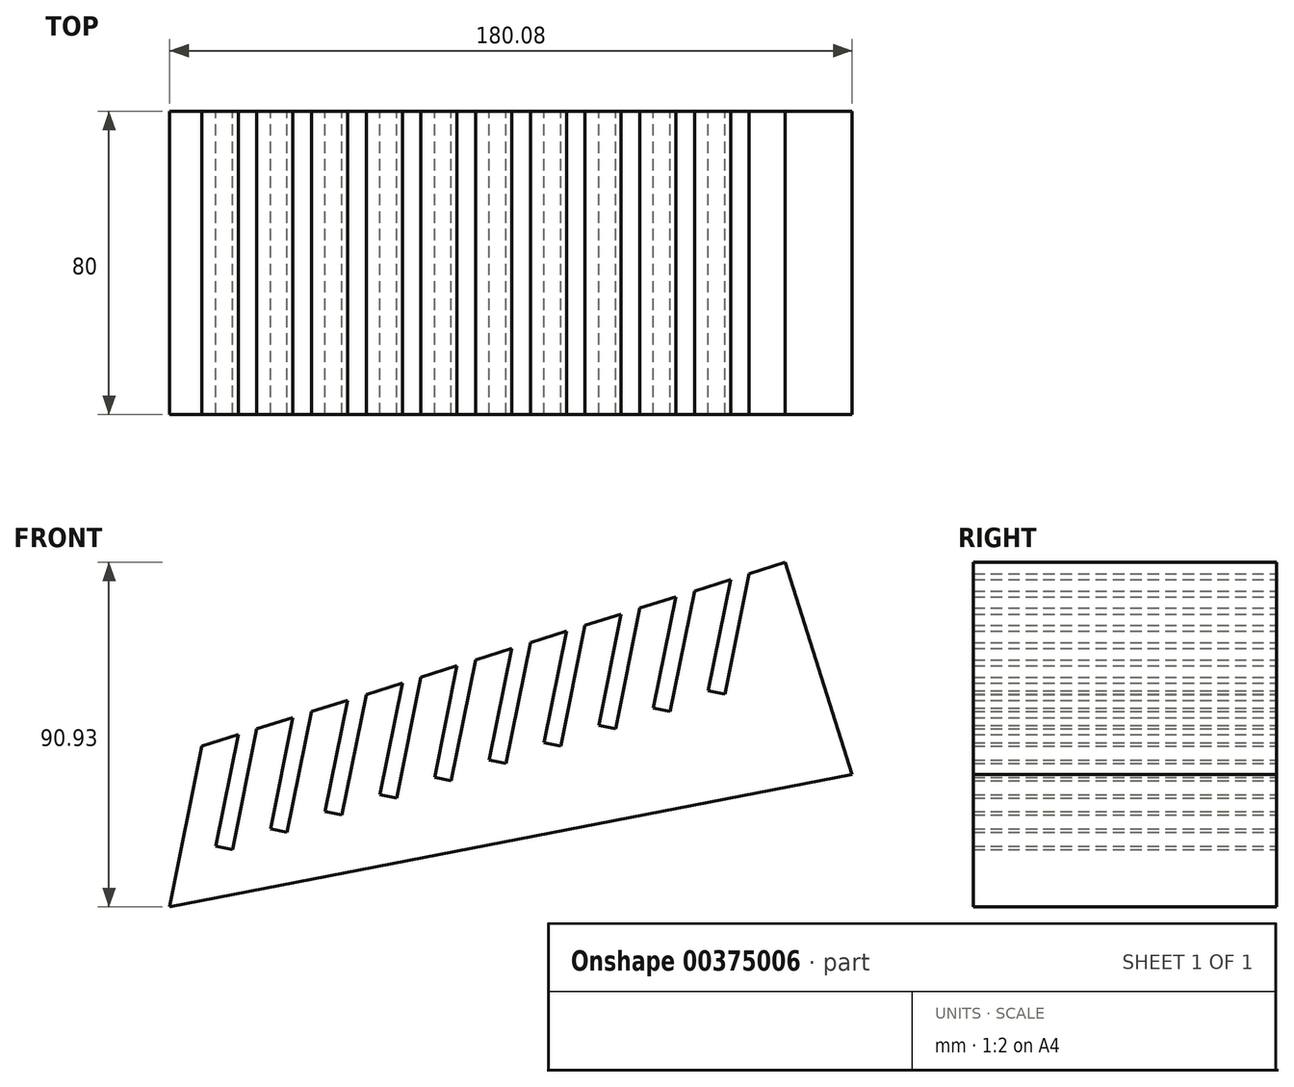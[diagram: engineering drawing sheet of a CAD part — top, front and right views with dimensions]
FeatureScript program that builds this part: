
annotation { "Feature Type Name" : "Feature", "Feature Type Description" : "" }
export const myFeature = defineFeature(function(context is Context, id is Id, definition is map)
    precondition{}
    {
        {
            var Q0;
            Q0=qCreatedBy(makeId("Front.planeOp"),FACE);
            var sketch = newSketch(context, id + "F0", { "sketchPlane" : qUnion([Q0])});
            skLineSegment(sketch, "E0", {"start": v(-99.6, -88.06) * mm, "end": v(-91.07, -45.66) * mm});
            skLineSegment(sketch, "E1", {"start": v(-91.07, -45.66) * mm, "end": v(-81.54, -42.65) * mm});
            skLineSegment(sketch, "E2", {"start": v(-81.54, -42.65) * mm, "end": v(-87.45, -72.06) * mm});
            skLineSegment(sketch, "E3", {"start": v(-87.45, -72.06) * mm, "end": v(-83.04, -72.95) * mm});
            skLineSegment(sketch, "E4", {"start": v(-83.04, -72.95) * mm, "end": v(-76.64, -41.1) * mm});
            skLineSegment(sketch, "E5", {"start": v(-76.64, -41.1) * mm, "end": v(-67.1, -38.1) * mm});
            skLineSegment(sketch, "E6", {"start": v(-67.1, -38.1) * mm, "end": v(-73.01, -67.51) * mm});
            skLineSegment(sketch, "E7", {"start": v(-73.01, -67.51) * mm, "end": v(-68.6, -68.4) * mm});
            skLineSegment(sketch, "E8", {"start": v(-68.6, -68.4) * mm, "end": v(-62.2, -36.55) * mm});
            skLineSegment(sketch, "E9", {"start": v(-62.2, -36.55) * mm, "end": v(-52.66, -33.55) * mm});
            skLineSegment(sketch, "E10", {"start": v(-52.66, -33.55) * mm, "end": v(-58.58, -62.96) * mm});
            skLineSegment(sketch, "E11", {"start": v(-58.58, -62.96) * mm, "end": v(-54.16, -63.85) * mm});
            skLineSegment(sketch, "E12", {"start": v(-54.16, -63.85) * mm, "end": v(-47.76, -32) * mm});
            skLineSegment(sketch, "E13", {"start": v(-47.76, -32) * mm, "end": v(-38.22, -29) * mm});
            skLineSegment(sketch, "E14", {"start": v(-38.22, -29) * mm, "end": v(-44.14, -58.4) * mm});
            skLineSegment(sketch, "E15", {"start": v(-44.14, -58.4) * mm, "end": v(-39.73, -59.3) * mm});
            skLineSegment(sketch, "E16", {"start": v(-39.73, -59.3) * mm, "end": v(-33.32, -27.45) * mm});
            skLineSegment(sketch, "E17", {"start": v(-33.32, -27.45) * mm, "end": v(-23.79, -24.44) * mm});
            skLineSegment(sketch, "E18", {"start": v(-23.79, -24.44) * mm, "end": v(-29.7, -53.85) * mm});
            skLineSegment(sketch, "E19", {"start": v(-29.7, -53.85) * mm, "end": v(-25.29, -54.74) * mm});
            skLineSegment(sketch, "E20", {"start": v(-25.29, -54.74) * mm, "end": v(-18.88, -22.9) * mm});
            skLineSegment(sketch, "E21", {"start": v(-18.88, -22.9) * mm, "end": v(-9.35, -19.9) * mm});
            skLineSegment(sketch, "E22", {"start": v(-9.35, -19.9) * mm, "end": v(-15.26, -49.3) * mm});
            skLineSegment(sketch, "E23", {"start": v(-15.26, -49.3) * mm, "end": v(-10.85, -50.19) * mm});
            skLineSegment(sketch, "E24", {"start": v(-10.85, -50.19) * mm, "end": v(-4.45, -18.35) * mm});
            skLineSegment(sketch, "E25", {"start": v(-4.45, -18.35) * mm, "end": v(5.1, -15.34) * mm});
            skLineSegment(sketch, "E26", {"start": v(5.1, -15.34) * mm, "end": v(-0.82, -44.75) * mm});
            skLineSegment(sketch, "E27", {"start": v(-0.82, -44.75) * mm, "end": v(3.59, -45.64) * mm});
            skLineSegment(sketch, "E28", {"start": v(3.59, -45.64) * mm, "end": v(10, -13.8) * mm});
            skLineSegment(sketch, "E29", {"start": v(10, -13.8) * mm, "end": v(19.53, -10.79) * mm});
            skLineSegment(sketch, "E30", {"start": v(19.53, -10.79) * mm, "end": v(13.61, -40.2) * mm});
            skLineSegment(sketch, "E31", {"start": v(13.61, -40.2) * mm, "end": v(18.03, -41.08) * mm});
            skLineSegment(sketch, "E32", {"start": v(18.03, -41.08) * mm, "end": v(24.43, -9.24) * mm});
            skLineSegment(sketch, "E33", {"start": v(24.43, -9.24) * mm, "end": v(33.97, -6.23) * mm});
            skLineSegment(sketch, "E34", {"start": v(33.97, -6.23) * mm, "end": v(28.05, -35.64) * mm});
            skLineSegment(sketch, "E35", {"start": v(28.05, -35.64) * mm, "end": v(32.46, -36.53) * mm});
            skLineSegment(sketch, "E36", {"start": v(32.46, -36.53) * mm, "end": v(38.87, -4.69) * mm});
            skLineSegment(sketch, "E37", {"start": v(38.87, -4.69) * mm, "end": v(48.4, -1.68) * mm});
            skLineSegment(sketch, "E38", {"start": v(48.4, -1.68) * mm, "end": v(42.49, -31.1) * mm});
            skLineSegment(sketch, "E39", {"start": v(42.49, -31.1) * mm, "end": v(46.9, -31.98) * mm});
            skLineSegment(sketch, "E40", {"start": v(46.9, -31.98) * mm, "end": v(53.3, -0.14) * mm});
            skLineSegment(sketch, "E41", {"start": v(53.3, -0.14) * mm, "end": v(62.84, 2.87) * mm});
            skLineSegment(sketch, "E42", {"start": v(62.84, 2.87) * mm, "end": v(80.48, -53.08) * mm});
            skLineSegment(sketch, "E43", {"start": v(-99.6, -88.06) * mm, "end": v(80.48, -53.08) * mm});
            skSolve(sketch);
        }
        {
            var Q0;
            Q0 = qSketchRegion(id + "F0", true);
            extrude(context, id + "F1", {"entities" : qUnion([Q0]), "depth" : 80 * mm});
        }
    });
